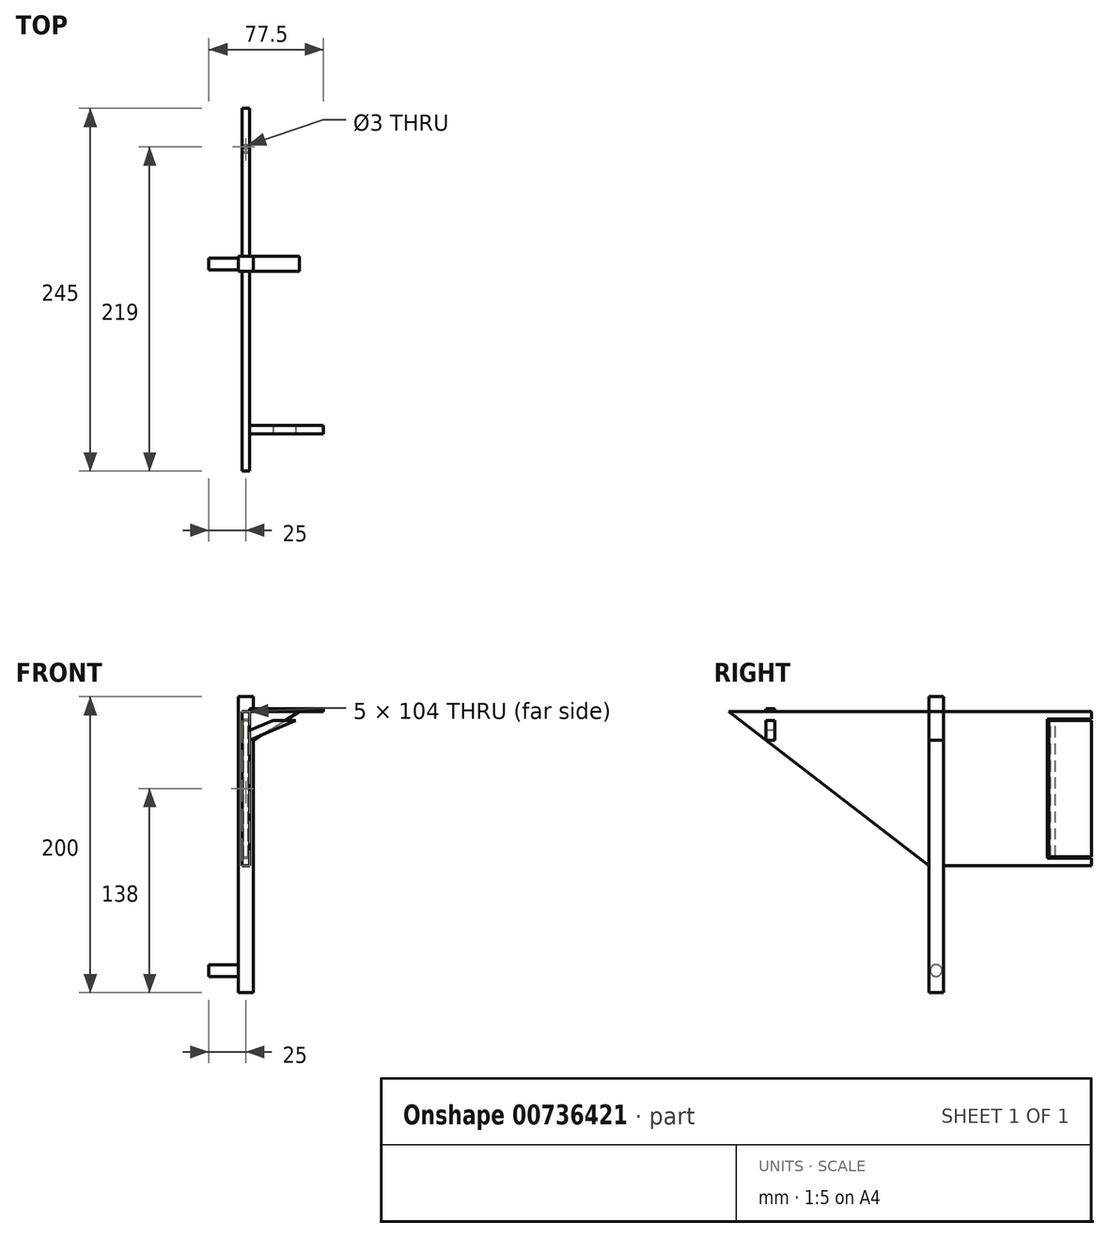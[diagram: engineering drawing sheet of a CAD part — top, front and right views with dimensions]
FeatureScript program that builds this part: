
annotation { "Feature Type Name" : "Feature", "Feature Type Description" : "" }
export const myFeature = defineFeature(function(context is Context, id is Id, definition is map)
    precondition{}
    {
        {
            var Q0;
            Q0=qCreatedBy(makeId("Front.planeOp"),FACE);
            var sketch = newSketch(context, id + "F0", { "sketchPlane" : qUnion([Q0])});
            skLineSegment(sketch, "E0.bottom", {"start": v(5, -100) * mm, "end": v(-5, -100) * mm});
            skLineSegment(sketch, "E0.top", {"start": v(5, 100) * mm, "end": v(-5, 100) * mm});
            skLineSegment(sketch, "E0.left", {"start": v(5, -100) * mm, "end": v(5, 100) * mm});
            skLineSegment(sketch, "E0.right", {"start": v(-5, -100) * mm, "end": v(-5, 100) * mm});
            skPoint(sketch, "E0.middle", {"position": v(0, 0) * mm});
            skSolve(sketch);
        }
        {
            var Q0;
            Q0=qSketchRegion(id+"F0",true);
            extrude(context, id + "F1", {"entities" : qUnion([Q0]), "depth" : 10 * mm, "offsetDistance" : 25 * mm});
        }
        {
            var Q0;
            Q0=makeQuery(id+"F1.opExtrude","CAP_FACE",FACE,{"disambiguationData":[OSD([sQuery(id+"F0.wireOp",EDGE,"E0.bottom"),sQuery(id+"F0.wireOp",EDGE,"E0.top"),sQuery(id+"F0.wireOp",EDGE,"E0.left"),sQuery(id+"F0.wireOp",EDGE,"E0.right")])],"isStart":false});
            var sketch = newSketch(context, id + "F2", { "sketchPlane" : qUnion([Q0])});
            skLineSegment(sketch, "E1", {"start": v(0, 90) * mm, "end": v(2.5, 90) * mm});
            skLineSegment(sketch, "E2", {"start": v(2.5, 90) * mm, "end": v(2.5, -14) * mm});
            skLineSegment(sketch, "E3", {"start": v(2.5, -14) * mm, "end": v(0, -14) * mm});
            skLineSegment(sketch, "E4", {"start": v(0, -14) * mm, "end": v(-2.5, -14) * mm});
            skLineSegment(sketch, "E5", {"start": v(-2.5, -14) * mm, "end": v(-2.5, 90) * mm});
            skLineSegment(sketch, "E6", {"start": v(-2.5, 90) * mm, "end": v(0, 90) * mm});
            skSolve(sketch);
        }
        {
            var Q0;
            Q0=qSketchRegion(id+"F2",true);
            extrude(context, id + "F3", {"entities" : qUnion([Q0]), "operationType" : NewBodyOperationType.ADD, "depth" : 135 * mm, "offsetDistance" : 25 * mm});
        }
        {
            var Q0;
            Q0=makeQuery(id+"F3.opExtrude","SWEPT_FACE",FACE,{"disambiguationData":[OSD([sQuery(id+"F2.wireOp",EDGE,"E2")])]});
            var sketch = newSketch(context, id + "F4", { "sketchPlane" : qUnion([Q0])});
            skLineSegment(sketch, "E7", {"start": v(-145, 90) * mm, "end": v(-145, -14) * mm});
            skLineSegment(sketch, "E8", {"start": v(-145, -14) * mm, "end": v(-10, -14) * mm});
            skLineSegment(sketch, "E9", {"start": v(-10, -14) * mm, "end": v(-145, 90) * mm});
            skSolve(sketch);
        }
        {
            var Q0;
            Q0=qSketchRegion(id+"F4",true);
            extrude(context, id + "F5", {"entities" : qUnion([Q0]), "operationType" : NewBodyOperationType.REMOVE, "endBound" : BoundingType.THROUGH_ALL, "oppositeDirection" : true, "depth" : 25 * mm, "offsetDistance" : 25 * mm});
        }
        {
            var Q0;
            Q0=makeQuery(id+"F1.opExtrude","SWEPT_FACE",FACE,{"disambiguationData":[OSD([sQuery(id+"F0.wireOp",EDGE,"E0.right")])]});
            var sketch = newSketch(context, id + "F6", { "sketchPlane" : qUnion([Q0])});
            skLineSegment(sketch, "E10", {"start": v(5, 100) * mm, "end": v(5, 45.97) * mm});
            skLineSegment(sketch, "E11", {"start": v(5, 100) * mm, "end": v(5, 90) * mm});
            skLineSegment(sketch, "E12", {"start": v(5, 90) * mm, "end": v(5, 70.75) * mm});
            skLineSegment(sketch, "E13", {"start": v(5, 70.75) * mm, "end": v(10, 70.75) * mm});
            skLineSegment(sketch, "E14", {"start": v(10, 70.75) * mm, "end": v(10, 80.75) * mm});
            skLineSegment(sketch, "E15", {"start": v(10, 80.75) * mm, "end": v(0, 80.75) * mm});
            skLineSegment(sketch, "E16", {"start": v(0, 80.75) * mm, "end": v(0, 70.75) * mm});
            skLineSegment(sketch, "E17", {"start": v(0, 70.75) * mm, "end": v(5, 70.75) * mm});
            skLineSegment(sketch, "E18", {"start": v(10, 80.75) * mm, "end": v(10, 90) * mm});
            skLineSegment(sketch, "E19", {"start": v(10, 90) * mm, "end": v(0, 90) * mm});
            skLineSegment(sketch, "E20", {"start": v(0, 90) * mm, "end": v(0, 80.75) * mm});
            skSolve(sketch);
        }
        {
            var Q0;
            {var subQ0=sQuery(id+"F6.wireOp",EDGE,"E13");Q0=makeQuery(id+"F6.imprint","IMPRINT",FACE,{"disambiguationData":[TD([[makeQuery(id+"F6.imprint","IMPRINT",EDGE,{"derivedFrom":subQ0}),1.0]])]});}
            var Q1;
            {var subQ4=sQuery(id+"F6.wireOp",EDGE,"E16");Q1=makeQuery(id+"F6.imprint","IMPRINT",FACE,{"disambiguationData":[TD([[makeQuery(id+"F6.imprint","IMPRINT",EDGE,{"derivedFrom":subQ4}),-1.0]])]});}
            var Q2;
            {var subQ5=sQuery(id+"F6.wireOp",EDGE,"E20");Q2=makeQuery(id+"F6.imprint","IMPRINT",FACE,{"disambiguationData":[TD([[makeQuery(id+"F6.imprint","IMPRINT",EDGE,{"derivedFrom":subQ5}),-1.0]])]});}
            var Q3;
            {var subQ5=sQuery(id+"F6.wireOp",EDGE,"E18");Q3=makeQuery(id+"F6.imprint","IMPRINT",FACE,{"disambiguationData":[TD([[makeQuery(id+"F6.imprint","IMPRINT",EDGE,{"derivedFrom":subQ5}),1.0]])]});}
            var Q4;
            {var subQ0=sQuery(id+"F6.wireOp",EDGE,"E11");Q4=makeQuery(id+"F6.imprint","IMPRINT",FACE,{"disambiguationData":[TD([[makeQuery(id+"F6.imprint","IMPRINT",EDGE,{"derivedFrom":subQ0}),-1.0]])]});}
            var Q5;
            {var subQ0=sQuery(id+"F6.wireOp",EDGE,"E11");Q5=makeQuery(id+"F6.imprint","IMPRINT",FACE,{"disambiguationData":[TD([[makeQuery(id+"F6.imprint","IMPRINT",EDGE,{"derivedFrom":subQ0}),1.0]])]});}
            extrude(context, id + "F7", {"entities" : qUnion([Q0, Q1, Q2, Q3, Q4, Q5]), "operationType" : NewBodyOperationType.ADD, "oppositeDirection" : true, "depth" : 57.5 * mm, "offsetDistance" : 25 * mm});
        }
        {
            var Q0;
            Q0=makeQuery(id+"F1.opExtrude","SWEPT_FACE",FACE,{"disambiguationData":[OSD([sQuery(id+"F0.wireOp",EDGE,"E0.left")])]});
            var sketch = newSketch(context, id + "F8", { "sketchPlane" : qUnion([Q0])});
            skLineSegment(sketch, "E21", {"start": v(-5, -100) * mm, "end": v(-5, -85) * mm});
            skCircle(sketch, "E22", {"center": v(-5, -85) * mm, "radius": 4 * mm});
            skSolve(sketch);
        }
        {
            var Q0;
            Q0=makeQuery(id+"F8.imprint","IMPRINT",FACE,{"disambiguationData":[TD([[makeQuery(id+"F8.imprint","IMPRINT",EDGE,{"derivedFrom":sQuery(id+"F8.wireOp",EDGE,"E22")}),1.0]])]});
            extrude(context, id + "F9", {"entities" : qUnion([Q0]), "operationType" : NewBodyOperationType.ADD, "oppositeDirection" : true, "depth" : 30 * mm, "offsetDistance" : 25 * mm});
        }
        {
            var Q0;
            Q0=makeQuery(id+"F7.boolean.opBoolean","MERGE",FACE,{"derivedFrom":[makeQuery(id+"F1.opExtrude","CAP_FACE",FACE,{"disambiguationData":[OSD([sQuery(id+"F0.wireOp",EDGE,"E0.bottom"),sQuery(id+"F0.wireOp",EDGE,"E0.top"),sQuery(id+"F0.wireOp",EDGE,"E0.left"),sQuery(id+"F0.wireOp",EDGE,"E0.right")])],"isStart":true}),makeQuery(id+"F7.opExtrude","SWEPT_FACE",FACE,{"disambiguationData":[OSD([sQuery(id+"F6.wireOp",EDGE,"E16"),sQuery(id+"F6.wireOp",EDGE,"E20")])]})]});
            var sketch = newSketch(context, id + "F10", { "sketchPlane" : qUnion([Q0])});
            skLineSegment(sketch, "E23", {"start": v(0, 90) * mm, "end": v(2.5, 90) * mm});
            skLineSegment(sketch, "E24", {"start": v(0, 90) * mm, "end": v(-2.5, 90) * mm});
            skLineSegment(sketch, "E25.bottom", {"start": v(-2.5, 90) * mm, "end": v(2.5, 90) * mm});
            skLineSegment(sketch, "E25.top", {"start": v(-2.5, -14) * mm, "end": v(2.5, -14) * mm});
            skLineSegment(sketch, "E25.left", {"start": v(-2.5, 90) * mm, "end": v(-2.5, -14) * mm});
            skLineSegment(sketch, "E25.right", {"start": v(2.5, 90) * mm, "end": v(2.5, -14) * mm});
            skPoint(sketch, "E26.start.orphan", {"position": v(-23.75, 100) * mm});
            skSolve(sketch);
        }
        {
            var Q0;
            Q0=qSketchRegion(id+"F10",true);
            extrude(context, id + "F11", {"entities" : qUnion([Q0]), "operationType" : NewBodyOperationType.ADD, "depth" : 100 * mm, "offsetDistance" : 25 * mm});
        }
        {
            var Q0;
            Q0=makeQuery(id+"F11.opExtrude","SWEPT_FACE",FACE,{"disambiguationData":[OSD([sQuery(id+"F10.wireOp",EDGE,"E25.left")])]});
            var sketch = newSketch(context, id + "F12", { "sketchPlane" : qUnion([Q0])});
            skLineSegment(sketch, "E27", {"start": v(100, 85) * mm, "end": v(70, 85) * mm});
            skLineSegment(sketch, "E28", {"start": v(70, 85) * mm, "end": v(70, -9) * mm});
            skLineSegment(sketch, "E29", {"start": v(70, -9) * mm, "end": v(100, -9) * mm});
            skLineSegment(sketch, "E30", {"start": v(100, 85) * mm, "end": v(100, 84) * mm});
            skLineSegment(sketch, "E31", {"start": v(100, 84) * mm, "end": v(71, 84) * mm});
            skLineSegment(sketch, "E32", {"start": v(71, 84) * mm, "end": v(71, -8) * mm});
            skLineSegment(sketch, "E33", {"start": v(71, -8) * mm, "end": v(100, -8) * mm});
            skSolve(sketch);
        }
        {
            var Q0;
            Q0=makeQuery(id+"F12.imprint","IMPRINT",FACE,{"disambiguationData":[TD([[makeQuery(id+"F12.imprint","IMPRINT",EDGE,{"derivedFrom":sQuery(id+"F12.wireOp",EDGE,"E27")}),1.0]])]});
            var Q1;
            Q1=makeQuery(id+"F11.opExtrude","SWEPT_FACE",FACE,{"disambiguationData":[OSD([sQuery(id+"F10.wireOp",EDGE,"E25.right")])]});
            extrude(context, id + "F13", {"entities" : qUnion([Q0]), "operationType" : NewBodyOperationType.REMOVE, "endBound" : BoundingType.UP_TO_SURFACE, "oppositeDirection" : true, "depth" : 25 * mm, "endBoundEntityFace" : qUnion([Q1]), "offsetDistance" : 25 * mm});
        }
        {
            var Q0;
            Q0=makeQuery(id+"F13.boolean.opBoolean","COPY",FACE,{"derivedFrom":makeQuery(id+"F13.opExtrude","SWEPT_FACE",FACE,{"disambiguationData":[OSD([sQuery(id+"F12.wireOp",EDGE,"E31")])]})});
            var sketch = newSketch(context, id + "F14", { "sketchPlane" : qUnion([Q0])});
            skLineSegment(sketch, "E34", {"start": v(0, 71) * mm, "end": v(0, 74) * mm});
            skCircle(sketch, "E35", {"center": v(0, 74) * mm, "radius": 1.5 * mm});
            skSolve(sketch);
        }
        {
            var Q0;
            Q0=qSketchRegion(id+"F14",true);
            var Q1;
            Q1=makeQuery(id+"F13.boolean.opBoolean","COPY",FACE,{"derivedFrom":makeQuery(id+"F13.opExtrude","SWEPT_FACE",FACE,{"disambiguationData":[OSD([sQuery(id+"F12.wireOp",EDGE,"E33")])]})});
            extrude(context, id + "F15", {"entities" : qUnion([Q0]), "operationType" : NewBodyOperationType.REMOVE, "endBound" : BoundingType.UP_TO_SURFACE, "oppositeDirection" : true, "depth" : 25 * mm, "endBoundEntityFace" : qUnion([Q1]), "offsetDistance" : 25 * mm});
        }
        {
            var Q0;
            Q0=makeQuery(id+"F13.boolean.opBoolean","COPY",FACE,{"derivedFrom":makeQuery(id+"F13.opExtrude","SWEPT_FACE",FACE,{"disambiguationData":[OSD([sQuery(id+"F12.wireOp",EDGE,"E27")])]})});
            var sketch = newSketch(context, id + "F16", { "sketchPlane" : qUnion([Q0])});
            skLineSegment(sketch, "E36", {"start": v(0, -70) * mm, "end": v(0, -74) * mm});
            skCircle(sketch, "E37", {"center": v(0, -74) * mm, "radius": 1.5 * mm});
            skLineSegment(sketch, "E38", {"start": v(0, -100) * mm, "end": v(0, -70) * mm});
            skSolve(sketch);
        }
        {
            var Q0;
            Q0=qSketchRegion(id+"F16",true);
            var Q1;
            Q1=makeQuery(id+"F13.boolean.opBoolean","COPY",FACE,{"derivedFrom":makeQuery(id+"F13.opExtrude","SWEPT_FACE",FACE,{"disambiguationData":[OSD([sQuery(id+"F12.wireOp",EDGE,"E29")])]})});
            extrude(context, id + "F17", {"entities" : qUnion([Q0]), "endBound" : BoundingType.UP_TO_SURFACE, "depth" : 25 * mm, "endBoundEntityFace" : qUnion([Q1]), "offsetDistance" : 25 * mm});
        }
        {
            var Q0;
            Q0=makeQuery(id+"F7.boolean.opBoolean","MERGE",FACE,{"derivedFrom":[makeQuery(id+"F1.opExtrude","CAP_FACE",FACE,{"disambiguationData":[OSD([sQuery(id+"F0.wireOp",EDGE,"E0.bottom"),sQuery(id+"F0.wireOp",EDGE,"E0.top"),sQuery(id+"F0.wireOp",EDGE,"E0.left"),sQuery(id+"F0.wireOp",EDGE,"E0.right")])],"isStart":false}),makeQuery(id+"F7.opExtrude","SWEPT_FACE",FACE,{"disambiguationData":[OSD([sQuery(id+"F6.wireOp",EDGE,"E14"),sQuery(id+"F6.wireOp",EDGE,"E18")])]})]});
            var sketch = newSketch(context, id + "F18", { "sketchPlane" : qUnion([Q0])});
            skLineSegment(sketch, "E39", {"start": v(5, 70.75) * mm, "end": v(52.5, 100) * mm});
            skLineSegment(sketch, "E40", {"start": v(5, 70.75) * mm, "end": v(5, 70.75) * mm});
            skLineSegment(sketch, "E41", {"start": v(5, 70.75) * mm, "end": v(2.5, 70.75) * mm});
            skLineSegment(sketch, "E42", {"start": v(2.5, 90) * mm, "end": v(2.5, 100) * mm});
            skLineSegment(sketch, "E43", {"start": v(2.5, 100) * mm, "end": v(5, 100) * mm});
            skLineSegment(sketch, "E44", {"start": v(2.5, 90) * mm, "end": v(2.5, 82.33) * mm});
            skLineSegment(sketch, "E45", {"start": v(5, 70.75) * mm, "end": v(5, 100) * mm});
            skPoint(sketch, "E46.start.orphan", {"position": v(28.75, 85.37) * mm});
            skLineSegment(sketch, "E47", {"start": v(33.43, 100) * mm, "end": v(5, 82.5) * mm});
            skSolve(sketch);
        }
        {
            var Q0;
            {var subQ0=sQuery(id+"F18.wireOp",EDGE,"3nAFwRHE-Ulzs-Lr5r-Jccs-Sl9Q6PMFqJOp");var subQ6=sQuery(id+"F18.wireOp",EDGE,"E40");var subQ7=makeQuery(id+"F18.imprint","INTERSECT",VERTEX,{"derivedFrom":[subQ0,subQ6]});Q0=makeQuery(id+"F18.imprint","IMPRINT",FACE,{"disambiguationData":[TD([[makeQuery(id+"F18.imprint","IMPRINT",EDGE,{"disambiguationData":[TD([[subQ7,1.0]])],"derivedFrom":subQ0}),-1.0]])]});}
            var Q1;
            {var subQ0=sQuery(id+"F18.wireOp",EDGE,"E43");var subQ5=sQuery(id+"F18.wireOp",EDGE,"E45");var subQ7=makeQuery(id+"F18.imprint","INTERSECT",VERTEX,{"derivedFrom":[subQ0,subQ5]});Q1=makeQuery(id+"F18.imprint","IMPRINT",FACE,{"disambiguationData":[TD([[makeQuery(id+"F18.imprint","IMPRINT",EDGE,{"disambiguationData":[TD([[subQ7,1.0]])],"derivedFrom":subQ5}),-1.0]])]});}
            var Q2;
            Q2=makeQuery(id+"F18.imprint","IMPRINT",FACE,{"disambiguationData":[TD([[makeQuery(id+"F18.imprint","IMPRINT",EDGE,{"derivedFrom":sQuery(id+"F18.wireOp",EDGE,"E39")}),-1.0]])]});
            extrude(context, id + "F19", {"entities" : qUnion([Q0, Q1, Q2]), "operationType" : NewBodyOperationType.REMOVE, "oppositeDirection" : true, "depth" : 25 * mm, "offsetDistance" : 25 * mm});
        }
        {
            var Q0;
            {var subQ0=sQuery(id+"F10.wireOp",EDGE,"E25.left");var subQ2=sQuery(id+"F10.wireOp",EDGE,"E25.bottom");Q0=makeQuery(id+"F19.boolean.opBoolean","MERGE",FACE,{"derivedFrom":[makeQuery(id+"F3.opExtrude","SWEPT_FACE",FACE,{"disambiguationData":[OSD([sQuery(id+"F2.wireOp",EDGE,"E2")])]}),makeQuery(id+"F13.boolean.opBoolean","SPLIT",FACE,{"disambiguationData":[TD([makeQuery(id+"F11.opExtrude","SWEPT_FACE",FACE,{"disambiguationData":[OSD([subQ2])]})])],"derivedFrom":makeQuery(id+"F11.opExtrude","SWEPT_FACE",FACE,{"disambiguationData":[OSD([subQ0])]})}),makeQuery(id+"F19.opExtrude","SWEPT_FACE",FACE,{"disambiguationData":[OSD([sQuery(id+"F18.wireOp",EDGE,"E42"),sQuery(id+"F18.wireOp",EDGE,"E44")])]})]});}
            var sketch = newSketch(context, id + "F20", { "sketchPlane" : qUnion([Q0])});
            skLineSegment(sketch, "E48", {"start": v(-10, 90) * mm, "end": v(-114, 90) * mm});
            skLineSegment(sketch, "E49.bottom", {"start": v(-114, 90) * mm, "end": v(-120, 90) * mm});
            skLineSegment(sketch, "E49.top", {"start": v(-114, 92) * mm, "end": v(-120, 92) * mm});
            skLineSegment(sketch, "E49.left", {"start": v(-114, 90) * mm, "end": v(-114, 92) * mm});
            skLineSegment(sketch, "E49.right", {"start": v(-120, 90) * mm, "end": v(-120, 92) * mm});
            skLineSegment(sketch, "E50.bottom", {"start": v(-120, 90) * mm, "end": v(-114, 90) * mm});
            skLineSegment(sketch, "E50.top", {"start": v(-120, 84) * mm, "end": v(-114, 84) * mm});
            skLineSegment(sketch, "E50.left", {"start": v(-120, 90) * mm, "end": v(-120, 84) * mm});
            skLineSegment(sketch, "E50.right", {"start": v(-114, 90) * mm, "end": v(-114, 84) * mm});
            skLineSegment(sketch, "E51.top", {"start": v(-120, 76.75) * mm, "end": v(-114, 76.75) * mm});
            skLineSegment(sketch, "E51.left", {"start": v(-120, 84) * mm, "end": v(-120, 76.75) * mm});
            skLineSegment(sketch, "E51.right", {"start": v(-114, 84) * mm, "end": v(-114, 76.75) * mm});
            skLineSegment(sketch, "E52.top", {"start": v(-120, 70.75) * mm, "end": v(-114, 70.75) * mm});
            skLineSegment(sketch, "E52.left", {"start": v(-120, 76.75) * mm, "end": v(-120, 70.75) * mm});
            skLineSegment(sketch, "E52.right", {"start": v(-114, 76.75) * mm, "end": v(-114, 70.75) * mm});
            skLineSegment(sketch, "E53", {"start": v(-114, 70.75) * mm, "end": v(-10, 70.75) * mm});
            skSolve(sketch);
        }
        {
            var Q0;
            Q0=makeQuery(id+"F20.imprint","IMPRINT",FACE,{"disambiguationData":[TD([[makeQuery(id+"F20.imprint","IMPRINT",EDGE,{"derivedFrom":sQuery(id+"F20.wireOp",EDGE,"E51.top")}),-1.0]])]});
            var Q1;
            Q1=makeQuery(id+"F20.imprint","IMPRINT",FACE,{"disambiguationData":[TD([[makeQuery(id+"F20.imprint","IMPRINT",EDGE,{"derivedFrom":sQuery(id+"F20.wireOp",EDGE,"E50.top")}),-1.0]])]});
            var Q2;
            Q2=makeQuery(id+"F20.imprint","IMPRINT",FACE,{"disambiguationData":[TD([[makeQuery(id+"F20.imprint","IMPRINT",EDGE,{"derivedFrom":sQuery(id+"F20.wireOp",EDGE,"E50.bottom")}),-1.0]])]});
            var Q3;
            Q3=makeQuery(id+"F20.imprint","IMPRINT",FACE,{"disambiguationData":[TD([[makeQuery(id+"F20.imprint","IMPRINT",EDGE,{"derivedFrom":sQuery(id+"F20.wireOp",EDGE,"E49.top")}),1.0]])]});
            extrude(context, id + "F21", {"entities" : qUnion([Q0, Q1, Q2, Q3]), "operationType" : NewBodyOperationType.ADD, "depth" : 50 * mm, "offsetDistance" : 25 * mm});
        }
        {
            var Q0;
            Q0=makeQuery(id+"F21.opExtrude","SWEPT_FACE",FACE,{"disambiguationData":[OSD([sQuery(id+"F20.wireOp",EDGE,"E49.right"),sQuery(id+"F20.wireOp",EDGE,"E50.left"),sQuery(id+"F20.wireOp",EDGE,"E51.left"),sQuery(id+"F20.wireOp",EDGE,"E52.left")])]});
            var sketch = newSketch(context, id + "F22", { "sketchPlane" : qUnion([Q0])});
            skLineSegment(sketch, "E54", {"start": v(2.5, 70.75) * mm, "end": v(52.5, 92) * mm});
            skLineSegment(sketch, "E55", {"start": v(37.16, 92) * mm, "end": v(2.5, 77.27) * mm});
            skSolve(sketch);
        }
        {
            var Q0;
            Q0 = qSketchRegion(id + "F22", true);
            var Q1;
            {var subQ0=sQuery(id+"F22.wireOp",EDGE,"E55");Q1=makeQuery(id+"F22.imprint","IMPRINT",FACE,{"disambiguationData":[TD([[makeQuery(id+"F22.imprint","IMPRINT",EDGE,{"derivedFrom":subQ0}),-1.0]])]});}
            var Q2;
            Q2=makeQuery(id+"F22.imprint","IMPRINT",FACE,{"disambiguationData":[TD([[makeQuery(id+"F22.imprint","IMPRINT",EDGE,{"derivedFrom":sQuery(id+"F22.wireOp",EDGE,"E54")}),-1.0]])]});
            extrude(context, id + "F23", {"entities" : qUnion([Q0, Q1, Q2]), "operationType" : NewBodyOperationType.REMOVE, "oppositeDirection" : true, "depth" : 25 * mm, "offsetDistance" : 25 * mm});
        }
    });
